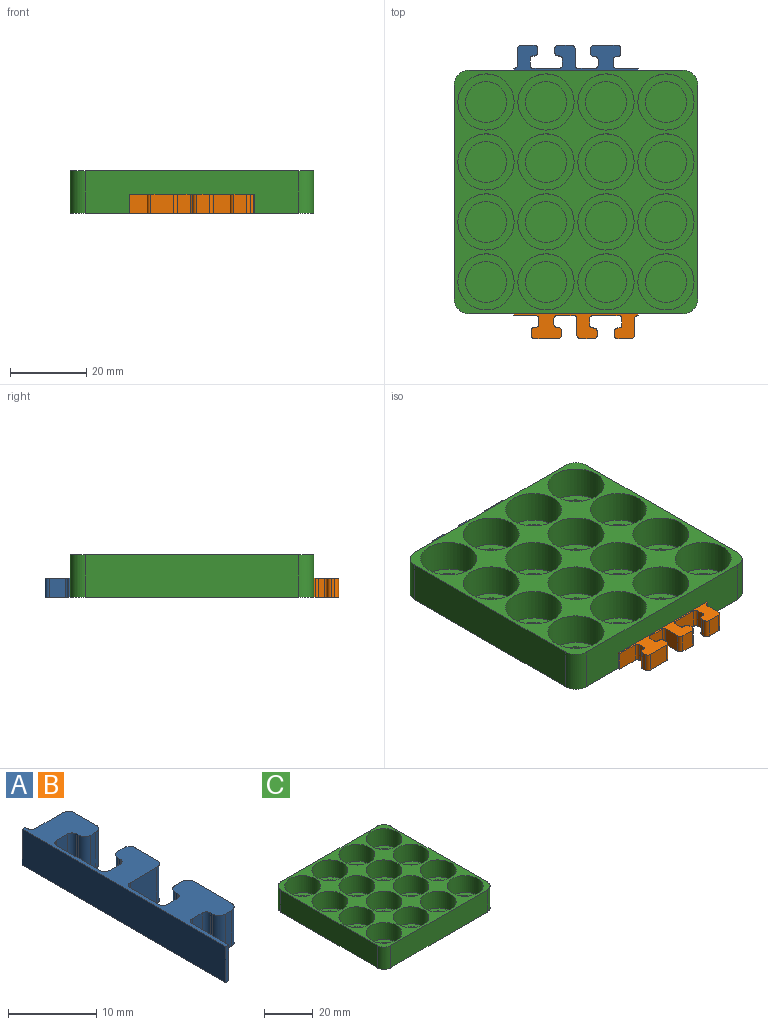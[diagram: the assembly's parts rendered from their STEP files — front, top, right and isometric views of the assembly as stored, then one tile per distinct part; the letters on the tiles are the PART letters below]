
ASSEMBLY  parts=3 mates=2
PART A: 46 faces, bbox 6.5x32.7x5 mm
  f0: plane 5x1.6mm, normal (0,1,0), area 8mm2, adj f24,f25,f38,f39
  f1: plane 5x4.57mm, normal (1,0,0), area 22.9mm2, adj f24,f25,f39,f43
  f2: plane 5x4.3mm, normal (0,-1,0), area 21.5mm2, adj f24,f25,f33,f43
  f3: plane 5x3.37mm, normal (1,0,0), area 16.9mm2, adj f24,f25,f33,f34
  f4: plane 5x0.8mm, normal (0,1,0), area 4mm2, adj f24,f25,f34,f35
  f5: plane 5x0.3mm, normal (-1,0,0), area 1.5mm2, adj f24,f25,f35,f45
  f6: plane 5x1.8mm, normal (0,1,0), area 9mm2, adj f24,f25,f44,f45
  f7: plane 7x5mm, normal (1,0,0), area 35mm2, adj f24,f25,f40,f44
  f8: plane 5x1.8mm, normal (0,-1,0), area 9mm2, adj f24,f25,f40,f41
  f9: plane 5x0.3mm, normal (-1,0,0), area 1.5mm2, adj f24,f25,f30,f41
  f10: plane 5x0.8mm, normal (0,-1,0), area 4mm2, adj f24,f25,f30,f31
  f11: plane 5x3.37mm, normal (1,0,0), area 16.9mm2, adj f24,f25,f31,f32
  f12: plane 5x4.3mm, normal (0,1,0), area 21.5mm2, adj f24,f25,f32,f42
  f13: plane 5x0.3mm, normal (1,0,0), area 1.5mm2, adj f14,f24,f25,f42
  f14: plane 5x0.5mm, normal (0,1,0), area 2.5mm2, adj f13,f15,f24,f25
  f15: plane 32.7x5mm, normal (-1,0,0), area 163.5mm2, adj f14,f16,f24,f25
  f16: plane 5x0.5mm, normal (0,-1,0), area 2.5mm2, adj f15,f17,f24,f25
  f17: plane 5.87x5mm, normal (1,0,0), area 29.4mm2, adj f16,f24,f25,f36
  f18: plane 5x1.6mm, normal (0,-1,0), area 8mm2, adj f24,f25,f36,f37
  f19: plane 5x0.3mm, normal (-1,0,0), area 1.5mm2, adj f24,f25,f26,f37
  f20: plane 5x1mm, normal (0,-1,0), area 5mm2, adj f24,f25,f26,f27
  f21: plane 6x5mm, normal (1,0,0), area 30mm2, adj f24,f25,f27,f28
  f22: plane 5x1mm, normal (0,1,0), area 5mm2, adj f24,f25,f28,f29
  f23: plane 5x0.3mm, normal (-1,0,0), area 1.5mm2, adj f24,f25,f29,f38
  f24: plane 32.7x6.5mm, normal (0,0,1), area 102.9mm2, adj f0,f1,f2,f3,f4,f5,f6,f7
  f25: plane 32.7x6.5mm, normal (0,0,-1), area 102.9mm2, adj f0,f1,f2,f3,f4,f5,f6,f7
  f26: cylinder r=1mm len=5mm, axis (0,0,-1), area 7.9mm2, adj f19,f20,f24,f25
  f27: cylinder r=1mm len=5mm, axis (0,0,-1), area 7.9mm2, adj f20,f21,f24,f25
  f28: cylinder r=1mm len=5mm, axis (0,0,-1), area 7.9mm2, adj f21,f22,f24,f25
  f29: cylinder r=1mm len=5mm, axis (0,0,-1), area 7.9mm2, adj f22,f23,f24,f25
  f30: cylinder r=1mm len=5mm, axis (0,0,-1), area 7.9mm2, adj f9,f10,f24,f25
  f31: cylinder r=1mm len=5mm, axis (0,0,-1), area 7.9mm2, adj f10,f11,f24,f25
  f32: cylinder r=1mm len=5mm, axis (0,0,-1), area 7.9mm2, adj f11,f12,f24,f25
  f33: cylinder r=1mm len=5mm, axis (0,0,-1), area 7.9mm2, adj f2,f3,f24,f25
  f34: cylinder r=1mm len=5mm, axis (0,0,-1), area 7.9mm2, adj f3,f4,f24,f25
  f35: cylinder r=1mm len=5mm, axis (0,0,-1), area 7.9mm2, adj f4,f5,f24,f25
  f36: cylinder r=0.7mm len=5mm, axis (0,0,-1), area 5.5mm2, adj f17,f18,f24,f25
  f37: cylinder r=0.7mm len=5mm, axis (0,0,1), area 5.5mm2, adj f18,f19,f24,f25
  f38: cylinder r=0.7mm len=5mm, axis (0,0,1), area 5.5mm2, adj f0,f23,f24,f25
  f39: cylinder r=0.7mm len=5mm, axis (0,0,-1), area 5.5mm2, adj f0,f1,f24,f25
  f40: cylinder r=0.7mm len=5mm, axis (0,0,-1), area 5.5mm2, adj f7,f8,f24,f25
  f41: cylinder r=0.7mm len=5mm, axis (0,0,1), area 5.5mm2, adj f8,f9,f24,f25
  f42: cylinder r=0.7mm len=5mm, axis (0,0,-1), area 5.5mm2, adj f12,f13,f24,f25
  f43: cylinder r=0.7mm len=5mm, axis (0,0,1), area 5.5mm2, adj f1,f2,f24,f25
  f44: cylinder r=0.7mm len=5mm, axis (0,0,1), area 5.5mm2, adj f6,f7,f24,f25
  f45: cylinder r=0.7mm len=5mm, axis (0,0,1), area 5.5mm2, adj f5,f6,f24,f25
PART B: same geometry as A
PART C: 74 faces, bbox 63.8x63.8x11.1 mm
  f0: plane 55.8x11.1mm, normal (-1,0,0), area 619.4mm2, adj f4,f21,f70,f73
  f1: plane 55.8x11.1mm, normal (0,-1,0), area 619.4mm2, adj f4,f21,f70,f71
  f2: plane 55.8x11.1mm, normal (1,0,0), area 619.4mm2, adj f4,f21,f71,f72
  f3: plane 55.8x11.1mm, normal (0,1,0), area 619.4mm2, adj f4,f21,f72,f73
  f4: plane 63.8x63.8mm, normal (0,0,-1), area 4056.7mm2, adj f0,f1,f2,f3,f70,f71,f72,f73
  f5: cylinder r=7.35mm len=14.7mm, axis (0,0,-1), area 392.5mm2, adj f21,f65
  f6: cylinder r=7.35mm len=14.7mm, axis (0,0,-1), area 392.5mm2, adj f21,f62
  f7: cylinder r=7.35mm len=14.7mm, axis (0,0,-1), area 392.5mm2, adj f21,f59
  f8: cylinder r=7.35mm len=14.7mm, axis (0,0,-1), area 392.5mm2, adj f21,f56
  f9: cylinder r=7.35mm len=14.7mm, axis (0,0,-1), area 392.5mm2, adj f21,f53
  f10: cylinder r=7.35mm len=14.7mm, axis (0,0,-1), area 392.5mm2, adj f21,f50
  f11: cylinder r=7.35mm len=14.7mm, axis (0,0,-1), area 392.5mm2, adj f21,f47
  f12: cylinder r=7.35mm len=14.7mm, axis (0,0,-1), area 392.5mm2, adj f21,f44
  f13: cylinder r=7.35mm len=14.7mm, axis (0,0,-1), area 392.5mm2, adj f21,f41
  f14: cylinder r=7.35mm len=14.7mm, axis (0,0,-1), area 392.5mm2, adj f21,f38
  f15: cylinder r=7.35mm len=14.7mm, axis (0,0,-1), area 392.5mm2, adj f21,f35
  f16: cylinder r=7.35mm len=14.7mm, axis (0,0,-1), area 392.5mm2, adj f21,f32
  f17: cylinder r=7.35mm len=14.7mm, axis (0,0,-1), area 392.5mm2, adj f21,f29
  f18: cylinder r=7.35mm len=14.7mm, axis (0,0,-1), area 392.5mm2, adj f21,f26
  f19: cylinder r=7.35mm len=14.7mm, axis (0,0,-1), area 392.5mm2, adj f21,f23
  f20: cylinder r=7.35mm len=14.7mm, axis (0,0,-1), area 392.5mm2, adj f21,f68
  f21: plane 63.8x63.8mm, normal (0,0,1), area 1341.2mm2, adj f0,f1,f2,f3,f5,f6,f7,f8
  f22: cylinder r=5.35mm len=10.7mm, axis (0,0,-1), area 50.4mm2, adj f23,f24
  f23: plane 14.7x14.7mm, normal (0,0,1), area 79.8mm2, adj f19,f22
  f24: plane 10.7x10.7mm, normal (0,0,1), area 89.9mm2, adj f22
  f25: cylinder r=5.35mm len=10.7mm, axis (0,0,-1), area 50.4mm2, adj f26,f27
  f26: plane 14.7x14.7mm, normal (0,0,1), area 79.8mm2, adj f18,f25
  f27: plane 10.7x10.7mm, normal (0,0,1), area 89.9mm2, adj f25
  f28: cylinder r=5.35mm len=10.7mm, axis (0,0,-1), area 50.4mm2, adj f29,f30
  f29: plane 14.7x14.7mm, normal (0,0,1), area 79.8mm2, adj f17,f28
  f30: plane 10.7x10.7mm, normal (0,0,1), area 89.9mm2, adj f28
  f31: cylinder r=5.35mm len=10.7mm, axis (0,0,-1), area 50.4mm2, adj f32,f33
  f32: plane 14.7x14.7mm, normal (0,0,1), area 79.8mm2, adj f16,f31
  f33: plane 10.7x10.7mm, normal (0,0,1), area 89.9mm2, adj f31
  f34: cylinder r=5.35mm len=10.7mm, axis (0,0,-1), area 50.4mm2, adj f35,f36
  f35: plane 14.7x14.7mm, normal (0,0,1), area 79.8mm2, adj f15,f34
  f36: plane 10.7x10.7mm, normal (0,0,1), area 89.9mm2, adj f34
  f37: cylinder r=5.35mm len=10.7mm, axis (0,0,-1), area 50.4mm2, adj f38,f39
  f38: plane 14.7x14.7mm, normal (0,0,1), area 79.8mm2, adj f14,f37
  f39: plane 10.7x10.7mm, normal (0,0,1), area 89.9mm2, adj f37
  f40: cylinder r=5.35mm len=10.7mm, axis (0,0,-1), area 50.4mm2, adj f41,f42
  f41: plane 14.7x14.7mm, normal (0,0,1), area 79.8mm2, adj f13,f40
  f42: plane 10.7x10.7mm, normal (0,0,1), area 89.9mm2, adj f40
  f43: cylinder r=5.35mm len=10.7mm, axis (0,0,-1), area 50.4mm2, adj f44,f45
  f44: plane 14.7x14.7mm, normal (0,0,1), area 79.8mm2, adj f12,f43
  f45: plane 10.7x10.7mm, normal (0,0,1), area 89.9mm2, adj f43
  f46: cylinder r=5.35mm len=10.7mm, axis (0,0,-1), area 50.4mm2, adj f47,f48
  f47: plane 14.7x14.7mm, normal (0,0,1), area 79.8mm2, adj f11,f46
  f48: plane 10.7x10.7mm, normal (0,0,1), area 89.9mm2, adj f46
  f49: cylinder r=5.35mm len=10.7mm, axis (0,0,-1), area 50.4mm2, adj f50,f51
  f50: plane 14.7x14.7mm, normal (0,0,1), area 79.8mm2, adj f10,f49
  f51: plane 10.7x10.7mm, normal (0,0,1), area 89.9mm2, adj f49
  f52: cylinder r=5.35mm len=10.7mm, axis (0,0,-1), area 50.4mm2, adj f53,f54
  f53: plane 14.7x14.7mm, normal (0,0,1), area 79.8mm2, adj f9,f52
  f54: plane 10.7x10.7mm, normal (0,0,1), area 89.9mm2, adj f52
  f55: cylinder r=5.35mm len=10.7mm, axis (0,0,-1), area 50.4mm2, adj f56,f57
  f56: plane 14.7x14.7mm, normal (0,0,1), area 79.8mm2, adj f8,f55
  f57: plane 10.7x10.7mm, normal (0,0,1), area 89.9mm2, adj f55
  f58: cylinder r=5.35mm len=10.7mm, axis (0,0,-1), area 50.4mm2, adj f59,f60
  f59: plane 14.7x14.7mm, normal (0,0,1), area 79.8mm2, adj f7,f58
  f60: plane 10.7x10.7mm, normal (0,0,1), area 89.9mm2, adj f58
  f61: cylinder r=5.35mm len=10.7mm, axis (0,0,-1), area 50.4mm2, adj f62,f63
  f62: plane 14.7x14.7mm, normal (0,0,1), area 79.8mm2, adj f6,f61
  f63: plane 10.7x10.7mm, normal (0,0,1), area 89.9mm2, adj f61
  f64: cylinder r=5.35mm len=10.7mm, axis (0,0,-1), area 50.4mm2, adj f65,f66
  f65: plane 14.7x14.7mm, normal (0,0,1), area 79.8mm2, adj f5,f64
  f66: plane 10.7x10.7mm, normal (0,0,1), area 89.9mm2, adj f64
  f67: cylinder r=5.35mm len=10.7mm, axis (0,0,-1), area 50.4mm2, adj f68,f69
  f68: plane 14.7x14.7mm, normal (0,0,1), area 79.8mm2, adj f20,f67
  f69: plane 10.7x10.7mm, normal (0,0,1), area 89.9mm2, adj f67
  f70: cylinder r=4mm len=11.1mm, axis (0,0,-1), area 69.7mm2, adj f0,f1,f4,f21
  f71: cylinder r=4mm len=11.1mm, axis (0,0,1), area 69.7mm2, adj f1,f2,f4,f21
  f72: cylinder r=4mm len=11.1mm, axis (0,0,-1), area 69.7mm2, adj f2,f3,f4,f21
  f73: cylinder r=4mm len=11.1mm, axis (0,0,1), area 69.7mm2, adj f0,f3,f4,f21
PLACE A rot(axis=(0,0,1),90deg) t=(23.28,41.65,4.83)mm
PLACE B rot(axis=(0,0,-1),90deg) t=(23.28,-22.15,4.83)mm
PLACE C t=(-8.62,-22.15,5.93)mm fixed
MATE fastened C.f3 <-> A.f15  axis (0,1,0) through (23.28,41.65,4.83)mm
MATE fastened C.f1 <-> B.f15  axis (0,-1,0) through (23.28,-22.15,4.83)mm
